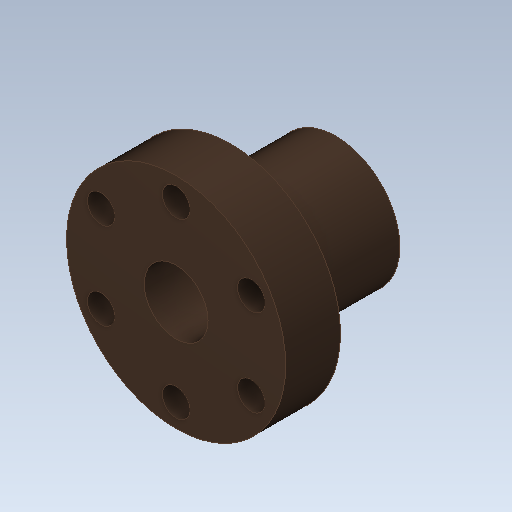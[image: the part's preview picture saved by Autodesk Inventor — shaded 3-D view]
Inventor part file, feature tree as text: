
AUTODESK INVENTOR PART (.ipt)
format: ipt  version: 2020 (Build 240168000, 168)  size: 137,216 bytes
history: native  units: mm
features: extrude x3, sketch x3, other x1, pattern_circular x1
ambient origin geometry x8: Origin, YZ Plane, XZ Plane, XY Plane, X Axis, Y Axis, Z Axis, Center Point
bodies: Body1 (feature_tree)
feature tree (8):
  other  "Bryła1"
  extrude  "Wyciągnięcie proste1"  Depth=48.0mm
  extrude  "Wyciągnięcie proste2"  Depth=28.0mm
  pattern_circular  "Szyk kołowy1"  [2 undecoded]
  extrude  "Wyciągnięcie proste3"  Depth=38.0mm
  sketch  "Szkic1"
  sketch  "Szkic2"
  sketch  "Szkic3"
note: 2 required parameter values undecoded (feature->parameter linkage not recoverable at this tier; creation-order binding heuristic only, values carry confidence <= 0.55)
